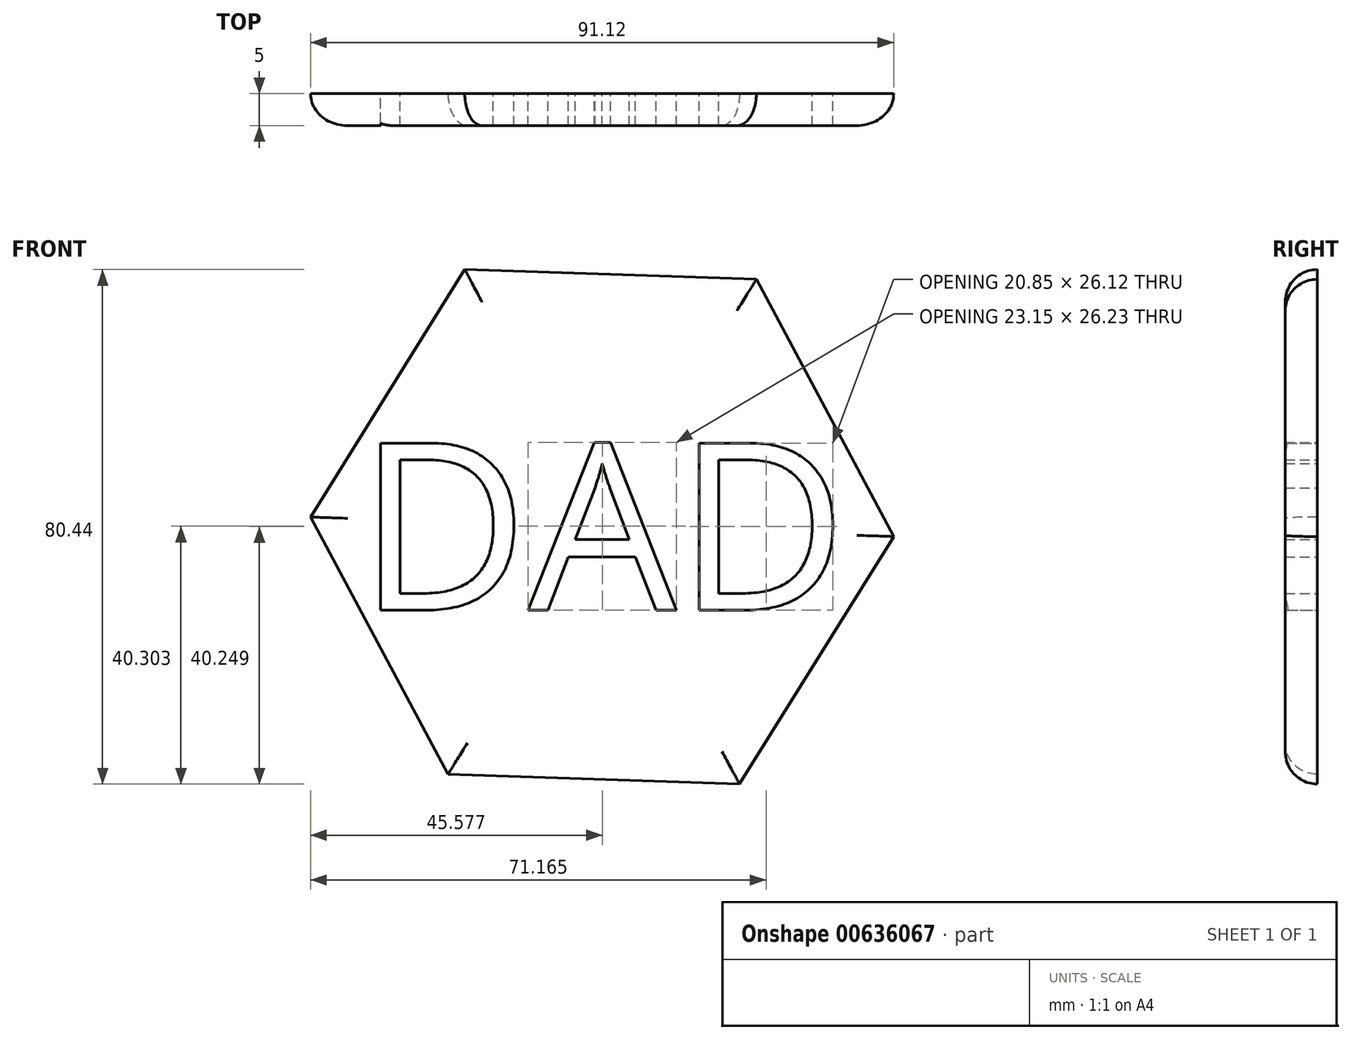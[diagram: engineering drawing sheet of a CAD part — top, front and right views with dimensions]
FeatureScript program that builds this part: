
annotation { "Feature Type Name" : "Feature", "Feature Type Description" : "" }
export const myFeature = defineFeature(function(context is Context, id is Id, definition is map)
    precondition{}
    {
        {
            var Q0;
            Q0=qCreatedBy(makeId("Front.planeOp"),FACE);
            var sketch = newSketch(context, id + "F0", { "sketchPlane" : qUnion([Q0])});
            skCircle(sketch, "E0.cCircle", {"center": v(0, 0) * mm, "radius": 39.48 * mm, "construction": true});
            skLineSegment(sketch, "E0.0", {"start": v(24.1, 38.7) * mm, "end": v(45.56, -1.52) * mm});
            skLineSegment(sketch, "E0.1", {"start": v(45.56, -1.52) * mm, "end": v(21.46, -40.22) * mm});
            skLineSegment(sketch, "E0.2", {"start": v(21.46, -40.22) * mm, "end": v(-24.1, -38.7) * mm});
            skLineSegment(sketch, "E0.3", {"start": v(-24.1, -38.7) * mm, "end": v(-45.56, 1.52) * mm});
            skLineSegment(sketch, "E0.4", {"start": v(-45.56, 1.52) * mm, "end": v(-21.46, 40.22) * mm});
            skLineSegment(sketch, "E0.5", {"start": v(-21.46, 40.22) * mm, "end": v(24.1, 38.7) * mm});
            skPoint(sketch, "E0.0.midPoint", {"position": v(34.83, 18.59) * mm});
            skText(sketch, "E1", { "text": "DAD", "fontName": "OpenSans-Regular.ttf"});
            const initialGuessF0  = {"E1": [-0.03823, -0.01303, 1, 0, 0.02634]};
            skSetInitialGuess(sketch, initialGuessF0);
            skSolve(sketch);
        }
        {
            var Q0;
            Q0=makeQuery(id+"F0.imprint","IMPRINT",FACE,{"disambiguationData":[TD([[makeQuery(id+"F0.imprint","IMPRINT",EDGE,{"derivedFrom":sQuery(id+"F0.wireOp",EDGE,"E1.sketch_text.stroke-22")}),1.0]])]});
            var Q1;
            Q1=makeQuery(id+"F0.imprint","IMPRINT",FACE,{"disambiguationData":[TD([[makeQuery(id+"F0.imprint","IMPRINT",EDGE,{"derivedFrom":sQuery(id+"F0.wireOp",EDGE,"E1.sketch_text.stroke-34")}),1.0]])]});
            var Q2;
            Q2=makeQuery(id+"F0.imprint","IMPRINT",FACE,{"disambiguationData":[TD([[makeQuery(id+"F0.imprint","IMPRINT",EDGE,{"derivedFrom":sQuery(id+"F0.wireOp",EDGE,"E0.0")}),-1.0]])]});
            var Q3;
            Q3=makeQuery(id+"F0.imprint","IMPRINT",FACE,{"disambiguationData":[TD([[makeQuery(id+"F0.imprint","IMPRINT",EDGE,{"derivedFrom":sQuery(id+"F0.wireOp",EDGE,"E1.sketch_text.stroke-7")}),1.0]])]});
            extrude(context, id + "F1", {"entities" : qUnion([Q0, Q1, Q2, Q3]), "depth" : 5 * mm, "offsetDistance" : 25 * mm});
        }
        {
            var Q0;
            Q0=makeQuery(id+"F1.opExtrude","CAP_EDGE",EDGE,{"disambiguationData":[OSD([sQuery(id+"F0.wireOp",EDGE,"E0.4")])],"isStart":false});
            var Q1;
            Q1=makeQuery(id+"F1.opExtrude","CAP_EDGE",EDGE,{"disambiguationData":[OSD([sQuery(id+"F0.wireOp",EDGE,"E0.5")])],"isStart":false});
            var Q2;
            Q2=makeQuery(id+"F1.opExtrude","CAP_EDGE",EDGE,{"disambiguationData":[OSD([sQuery(id+"F0.wireOp",EDGE,"E0.0")])],"isStart":false});
            var Q3;
            Q3=makeQuery(id+"F1.opExtrude","CAP_EDGE",EDGE,{"disambiguationData":[OSD([sQuery(id+"F0.wireOp",EDGE,"E0.1")])],"isStart":false});
            var Q4;
            Q4=makeQuery(id+"F1.opExtrude","CAP_EDGE",EDGE,{"disambiguationData":[OSD([sQuery(id+"F0.wireOp",EDGE,"E0.3")])],"isStart":false});
            var Q5;
            Q5=makeQuery(id+"F1.opExtrude","CAP_EDGE",EDGE,{"disambiguationData":[OSD([sQuery(id+"F0.wireOp",EDGE,"E0.2")])],"isStart":false});
            fillet(context, id + "F2", {"entities" : qUnion([Q0, Q1, Q2, Q3, Q4, Q5]), "radius" : 5 * mm, "tangentPropagation" : true, "allowEdgeOverflow" : false});
        }
    });
